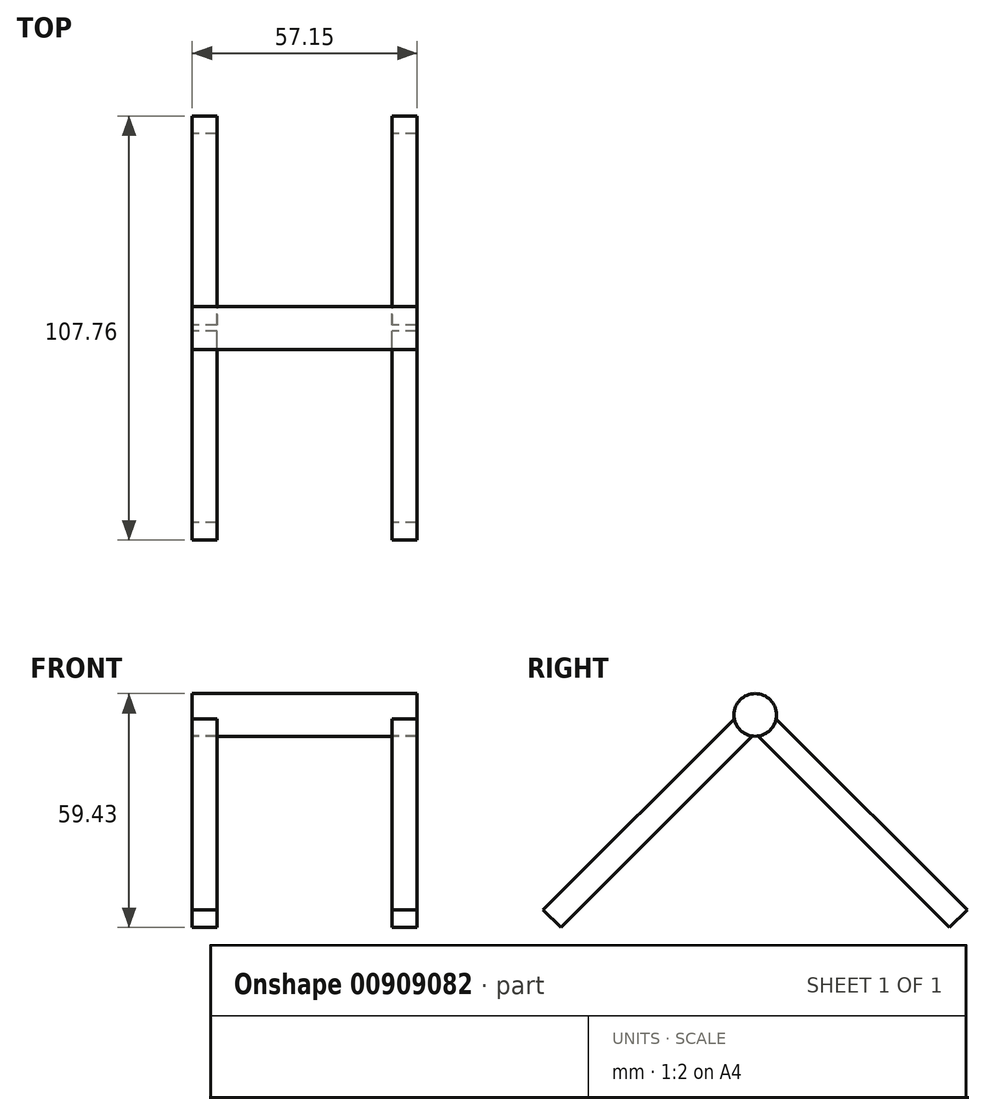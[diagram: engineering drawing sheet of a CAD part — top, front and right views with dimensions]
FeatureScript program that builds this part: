
annotation { "Feature Type Name" : "Feature", "Feature Type Description" : "" }
export const myFeature = defineFeature(function(context is Context, id is Id, definition is map)
    precondition{}
    {
        {
            var Q0;
            Q0=qCreatedBy(makeId("Right.planeOp"),FACE);
            var sketch = newSketch(context, id + "F0", { "sketchPlane" : qUnion([Q0])});
            skLineSegment(sketch, "E0", {"start": v(5.32, -5.32) * mm, "end": v(53.88, -53.88) * mm});
            skLineSegment(sketch, "E1", {"start": v(-5.32, -5.32) * mm, "end": v(-53.88, -53.88) * mm});
            skLineSegment(sketch, "E2", {"start": v(53.88, -53.88) * mm, "end": v(49.4, -58.37) * mm});
            skLineSegment(sketch, "E3", {"start": v(-53.88, -53.88) * mm, "end": v(-49.4, -58.37) * mm});
            skLineSegment(sketch, "E4", {"start": v(49.4, -58.37) * mm, "end": v(0.74, -9.72) * mm});
            skLineSegment(sketch, "E5", {"start": v(-49.4, -58.37) * mm, "end": v(-0.74, -9.72) * mm});
            skCircle(sketch, "E6", {"center": v(0, -4.35) * mm, "radius": 5.41 * mm});
            skPoint(sketch, "E7.orphan", {"position": v(0, 0) * mm});
            skPoint(sketch, "E8.orphan", {"position": v(0, -8.98) * mm});
            skSolve(sketch);
        }
        {
            var Q0;
            {var subQ0=sQuery(id+"F0.wireOp",EDGE,"E1");Q0=makeQuery(id+"F0.imprint","IMPRINT",FACE,{"disambiguationData":[TD([[makeQuery(id+"F0.imprint","IMPRINT",EDGE,{"derivedFrom":subQ0}),1.0]])]});}
            var Q1;
            {var subQ0=sQuery(id+"F0.wireOp",EDGE,"E0");Q1=makeQuery(id+"F0.imprint","IMPRINT",FACE,{"disambiguationData":[TD([[makeQuery(id+"F0.imprint","IMPRINT",EDGE,{"derivedFrom":subQ0}),-1.0]])]});}
            extrude(context, id + "F1", {"entities" : qUnion([Q0, Q1]), "depth" : 6.35 * mm, "offsetDistance" : 25.4 * mm});
        }
        {
            var Q0;
            {var subQ0=sQuery(id+"F0.wireOp",EDGE,"E1");Q0=makeQuery(id+"F0.imprint","IMPRINT",FACE,{"disambiguationData":[TD([[makeQuery(id+"F0.imprint","IMPRINT",EDGE,{"derivedFrom":subQ0}),1.0]])]});}
            var Q1;
            {var subQ0=sQuery(id+"F0.wireOp",EDGE,"E0");Q1=makeQuery(id+"F0.imprint","IMPRINT",FACE,{"disambiguationData":[TD([[makeQuery(id+"F0.imprint","IMPRINT",EDGE,{"derivedFrom":subQ0}),-1.0]])]});}
            extrude(context, id + "F2", {"entities" : qUnion([Q0, Q1]), "depth" : 57.15 * mm, "offsetDistance" : 25.4 * mm, "hasSecondDirection" : true, "secondDirectionOppositeDirection" : false, "secondDirectionDepth" : 50.8 * mm});
        }
        {
            var Q0;
            {var subQ0=sQuery(id+"F0.wireOp",EDGE,"E6");var subQ1=makeQuery(id+"F0.imprint","INTERSECT",VERTEX,{"derivedFrom":[sQuery(id+"F0.wireOp",EDGE,"E1"),subQ0]});Q0=makeQuery(id+"F0.imprint","IMPRINT",FACE,{"disambiguationData":[TD([[makeQuery(id+"F0.imprint","IMPRINT",EDGE,{"disambiguationData":[TD([[subQ1,-1.0]])],"derivedFrom":subQ0}),1.0]])]});}
            extrude(context, id + "F3", {"entities" : qUnion([Q0]), "depth" : 57.15 * mm, "offsetDistance" : 25.4 * mm});
        }
    });
